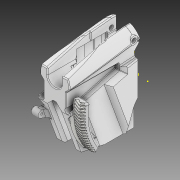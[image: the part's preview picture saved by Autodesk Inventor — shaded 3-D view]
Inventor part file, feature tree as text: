
AUTODESK INVENTOR PART (.ipt)
format: ipt  version: 2020 (Build 240168000, 168)  size: 3,878,912 bytes
history: native  units: in
note: dims shown in document units (in); Inventor stores cm internally (conversion verified against a paired STEP export)
features: sketch x10, extrude x9, fillet x4, other x3, chamfer x2, projected_geometry x2
ambient origin geometry x8: Origin, YZ Plane, XZ Plane, XY Plane, X Axis, Y Axis, Z Axis, Center Point
bodies: Solid1 (feature_tree)
feature tree (30):
  other  "GearedUpper.iam"
  other  "EUpper_Alt.ipt:1"
  other  "144 Tooth Herringbone semicircle.ipt:1"
  extrude  "Extrusion1"  Depth=0.0687in
  extrude  "Extrusion2"  Depth=1.0in TaperAngle=0.0deg
  extrude  "Extrusion3"  Depth=1.0in TaperAngle=0.0deg
  extrude  "Extrusion4"  Depth=1.0in TaperAngle=0.0deg
  extrude  "Extrusion5"  Depth=0.3937in TaperAngle=0.0deg
  extrude  "Extrusion6"  Depth=0.0787in
  fillet  "Fillet1"  Radius=3.4646in
  fillet  "Fillet2"  Radius=2.2047in
  sketch  "Sketch12"  dims[d29=0.315in]
  extrude  "Extrusion7"  Depth=1.7717in
  extrude  "Extrusion8"  Depth=1.9291in
  fillet  "Fillet3"  Radius=2.2835in
  fillet  "Fillet4"  Radius=0.0965in
  chamfer  "Chamfer1"  Distance=0.2756in
  extrude  "Extrusion9"  Depth=0.0394in TaperAngle=0.0deg
  chamfer  "Chamfer2"  Distance=0.0787in
  sketch  "Sketch4"  dims[d2=0.2405in d3=1.0in d4=0.0in]
  sketch  "Sketch9"  dims[d23=0.0756in d24=1.7717in]
  sketch  "Sketch3"  dims[d0=0.3937in d1=0.0687in]
  sketch  "Sketch5"  dims[d5=1.0in d6=0.0in d7=1.0in d8=0.0in]
  sketch  "Sketch6"  dims[d10=0.1575in d11=1.0in d12=0.0in]
  projected_geometry  "Projected Loop1"
  sketch  "Sketch7"  dims[d13=0.0in d14=0.0in d15=0.3937in d16=0.0in]
  sketch  "Sketch8"  dims[d17=0.1969in d18=0.0787in d21=3.4646in d22=2.2047in]
  sketch  "Sketch10"  dims[d25=2.7953in d26=1.9291in d27=2.2835in d28=0.0965in]
  projected_geometry  "Projected Loop2"
  sketch  "Sketch13"  dims[d30=0.315in d31=0.2756in d32=0.3937in d33=0.0in d34=0.0787in d35=0.5906in d36=0.1969in d37=0.0in d38=0.1575in d39=0.1181in d40=0.1181in d41=0.0591in d42=0.0787in d43=45.0deg d44=0.0394in d45=0.1969in d46=0.0in d47=0.0787in d48=0.0787in d49=45.0deg]
